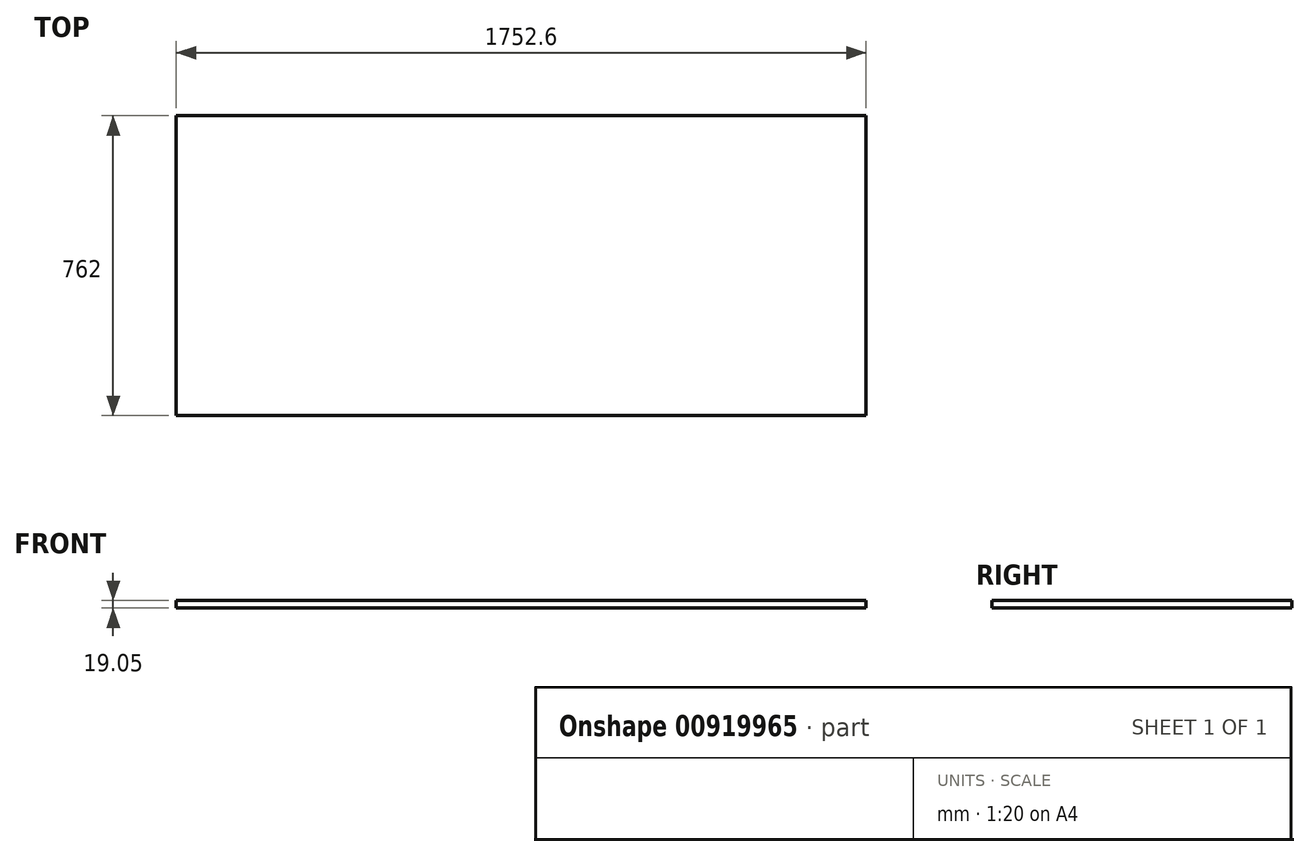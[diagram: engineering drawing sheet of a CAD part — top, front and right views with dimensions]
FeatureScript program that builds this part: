
annotation { "Feature Type Name" : "Feature", "Feature Type Description" : "" }
export const myFeature = defineFeature(function(context is Context, id is Id, definition is map)
    precondition{}
    {
        {
            var Q0;
            Q0=qCreatedBy(makeId("Top.planeOp"),FACE);
            var sketch = newSketch(context, id + "F0", { "sketchPlane" : qUnion([Q0])});
            skLineSegment(sketch, "E0.bottom", {"start": v(-876.3, 381) * mm, "end": v(876.3, 381) * mm});
            skLineSegment(sketch, "E0.top", {"start": v(-876.3, -381) * mm, "end": v(876.3, -381) * mm});
            skLineSegment(sketch, "E0.left", {"start": v(-876.3, 381) * mm, "end": v(-876.3, -381) * mm});
            skLineSegment(sketch, "E0.right", {"start": v(876.3, 381) * mm, "end": v(876.3, -381) * mm});
            skPoint(sketch, "E1", {"position": v(0, 381) * mm});
            skPoint(sketch, "E2", {"position": v(-876.3, 0) * mm});
            skSolve(sketch);
        }
        {
            var Q0;
            Q0=makeQuery(id+"F0.imprint","IMPRINT",FACE,{"disambiguationData":[TD([[makeQuery(id+"F0.imprint","IMPRINT",EDGE,{"derivedFrom":sQuery(id+"F0.wireOp",EDGE,"E0.bottom")}),-1.0]])]});
            extrude(context, id + "F1", {"entities" : qUnion([Q0]), "depth" : 19.05 * mm, "offsetDistance" : 25 * mm});
        }
    });
